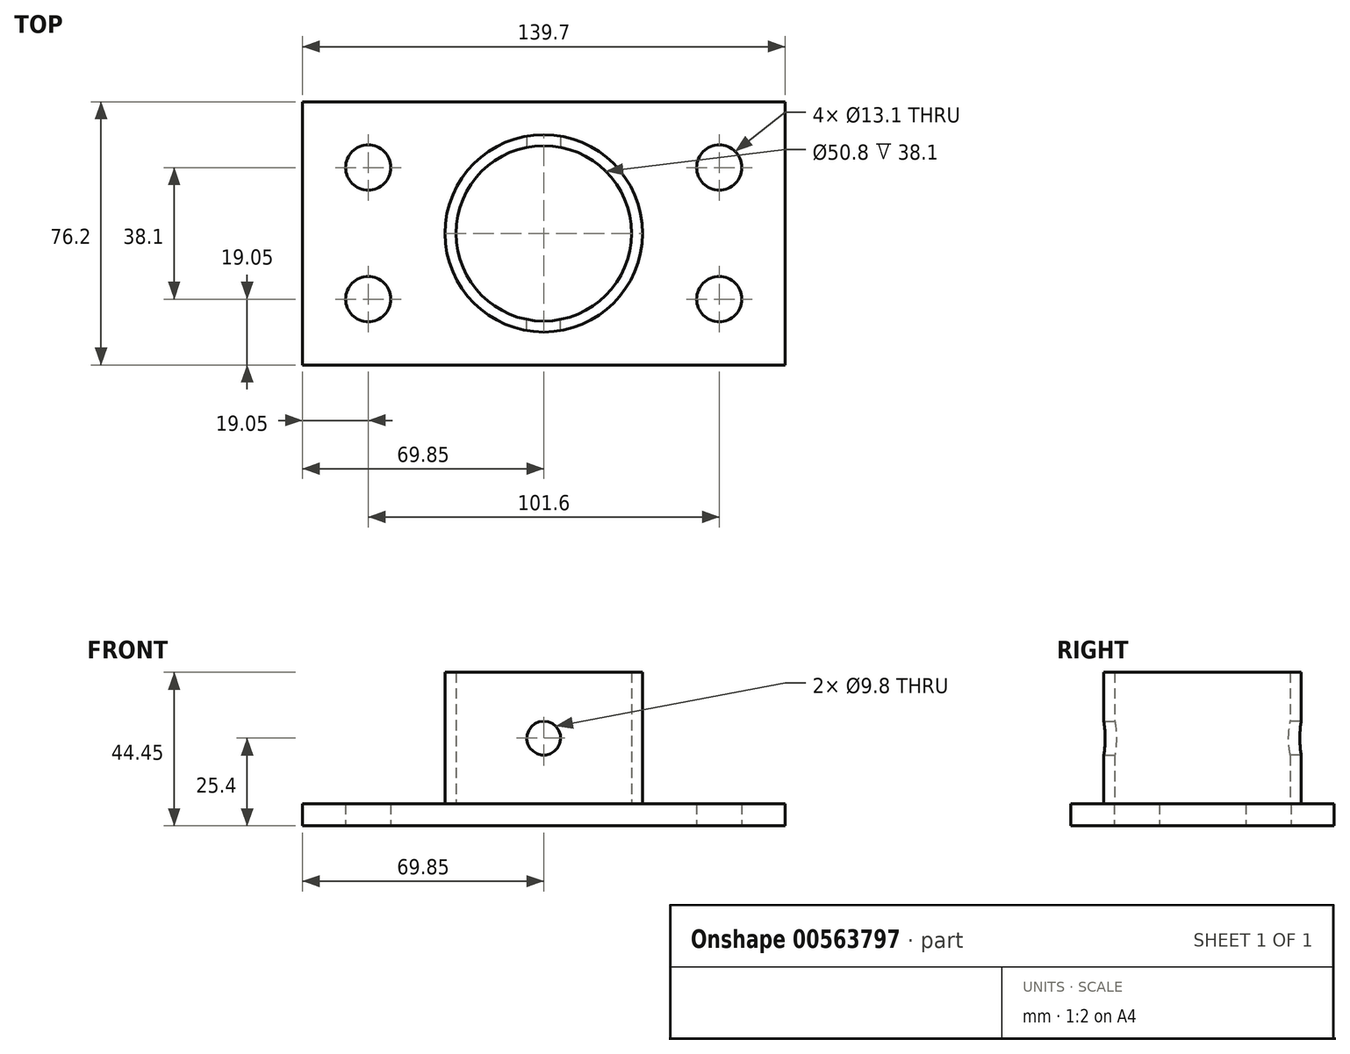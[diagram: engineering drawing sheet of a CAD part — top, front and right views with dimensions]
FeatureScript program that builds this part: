
annotation { "Feature Type Name" : "Feature", "Feature Type Description" : "" }
export const myFeature = defineFeature(function(context is Context, id is Id, definition is map)
    precondition{}
    {
        {
            var Q0;
            Q0=qCreatedBy(makeId("Top.planeOp"),FACE);
            var sketch = newSketch(context, id + "F0", { "sketchPlane" : qUnion([Q0])});
            skPoint(sketch, "E0", {"position": v(-50.8, 19.05) * mm});
            skPoint(sketch, "E1.MirrorP", {"position": v(-50.8, -19.05) * mm});
            skPoint(sketch, "E2.MirrorP", {"position": v(50.8, -19.05) * mm});
            skLineSegment(sketch, "E3.bottom", {"start": v(-69.85, 38.1) * mm, "end": v(69.85, 38.1) * mm});
            skLineSegment(sketch, "E3.top", {"start": v(-69.85, -38.1) * mm, "end": v(69.85, -38.1) * mm});
            skLineSegment(sketch, "E3.left", {"start": v(-69.85, 38.1) * mm, "end": v(-69.85, -38.1) * mm});
            skLineSegment(sketch, "E3.right", {"start": v(69.85, 38.1) * mm, "end": v(69.85, -38.1) * mm});
            skPoint(sketch, "E3.middle", {"position": v(0, 0) * mm});
            skPoint(sketch, "E4.MirrorP", {"position": v(50.8, 19.05) * mm});
            skCircle(sketch, "E5", {"center": v(0, 0) * mm, "radius": 28.58 * mm});
            skCircle(sketch, "E6", {"center": v(0, 0) * mm, "radius": 25.4 * mm});
            skSolve(sketch);
        }
        {
            var Q0;
            Q0=makeQuery(id+"F0.imprint","IMPRINT",FACE,{"disambiguationData":[TD([[makeQuery(id+"F0.imprint","IMPRINT",EDGE,{"derivedFrom":sQuery(id+"F0.wireOp",EDGE,"E6")}),1.0]])]});
            var Q1;
            Q1=makeQuery(id+"F0.imprint","IMPRINT",FACE,{"disambiguationData":[TD([[makeQuery(id+"F0.imprint","IMPRINT",EDGE,{"derivedFrom":sQuery(id+"F0.wireOp",EDGE,"E3.bottom")}),-1.0]])]});
            extrude(context, id + "F1", {"entities" : qUnion([Q0, Q1]), "depth" : 6.35 * mm, "offsetDistance" : 25.4 * mm});
        }
        {
            var Q0;
            Q0=makeQuery(id+"F0.imprint","IMPRINT",FACE,{"disambiguationData":[TD([[makeQuery(id+"F0.imprint","IMPRINT",EDGE,{"derivedFrom":sQuery(id+"F0.wireOp",EDGE,"E5")}),1.0]])]});
            extrude(context, id + "F2", {"entities" : qUnion([Q0]), "operationType" : NewBodyOperationType.ADD, "depth" : 44.45 * mm, "offsetDistance" : 25.4 * mm});
        }
        {
            var Q0;
            Q0=sQuery(id+"F0.wireOp",VERTEX,"E0");
            var Q1;
            Q1=sQuery(id+"F0.wireOp",VERTEX,"E4.MirrorP");
            var Q2;
            Q2=sQuery(id+"F0.wireOp",VERTEX,"E2.MirrorP");
            var Q3;
            Q3=sQuery(id+"F0.wireOp",VERTEX,"E1.MirrorP");
            var Q4;
            Q4=makeQuery(id+"F1.opExtrude","SWEPT_BODY",BODY,{"disambiguationData":[OSD([sQuery(id+"F0.wireOp",EDGE,"E3.bottom"),sQuery(id+"F0.wireOp",EDGE,"E3.top"),sQuery(id+"F0.wireOp",EDGE,"E3.left"),sQuery(id+"F0.wireOp",EDGE,"E3.right"),sQuery(id+"F0.wireOp",EDGE,"E5")])]});
            hole(context, id + "F3", {"style" : HoleStyle.SIMPLE, "endStyle" : HoleEndStyle.THROUGH, "oppositeDirection" : true, "holeDiameter" : 13.1 * mm, "isTappedThrough" : true, "tappedDepth" : 12.7 * mm, "tapClearance" : 3, "locations" : qUnion([Q0, Q1, Q2, Q3]), "scope" : qUnion([Q4])});
        }
        {
            var Q0;
            Q0=qCreatedBy(makeId("Front.planeOp"),FACE);
            var sketch = newSketch(context, id + "F4", { "sketchPlane" : qUnion([Q0])});
            skPoint(sketch, "E7", {"position": v(0, 25.4) * mm});
            skSolve(sketch);
        }
        {
            var Q0;
            Q0=sQuery(id+"F4.wireOp",VERTEX,"E7");
            var Q1;
            Q1=makeQuery(id+"F1.opExtrude","SWEPT_BODY",BODY,{"disambiguationData":[OSD([sQuery(id+"F0.wireOp",EDGE,"E3.bottom"),sQuery(id+"F0.wireOp",EDGE,"E3.top"),sQuery(id+"F0.wireOp",EDGE,"E3.left"),sQuery(id+"F0.wireOp",EDGE,"E3.right"),sQuery(id+"F0.wireOp",EDGE,"E5")])]});
            hole(context, id + "F5", {"style" : HoleStyle.SIMPLE, "endStyle" : HoleEndStyle.THROUGH, "oppositeDirection" : true, "holeDiameter" : 9.8 * mm, "isTappedThrough" : true, "tappedDepth" : 12.7 * mm, "tapClearance" : 3, "locations" : qUnion([Q0]), "scope" : qUnion([Q1])});
        }
        {
            var Q0;
            Q0=sQuery(id+"F4.wireOp",VERTEX,"E7");
            var Q1;
            Q1=makeQuery(id+"F1.opExtrude","SWEPT_BODY",BODY,{"disambiguationData":[OSD([sQuery(id+"F0.wireOp",EDGE,"E3.bottom"),sQuery(id+"F0.wireOp",EDGE,"E3.top"),sQuery(id+"F0.wireOp",EDGE,"E3.left"),sQuery(id+"F0.wireOp",EDGE,"E3.right"),sQuery(id+"F0.wireOp",EDGE,"E5")])]});
            hole(context, id + "F6", {"style" : HoleStyle.SIMPLE, "endStyle" : HoleEndStyle.THROUGH, "holeDiameter" : 9.8 * mm, "isTappedThrough" : true, "tappedDepth" : 12.7 * mm, "tapClearance" : 3, "locations" : qUnion([Q0]), "scope" : qUnion([Q1])});
        }
    });
